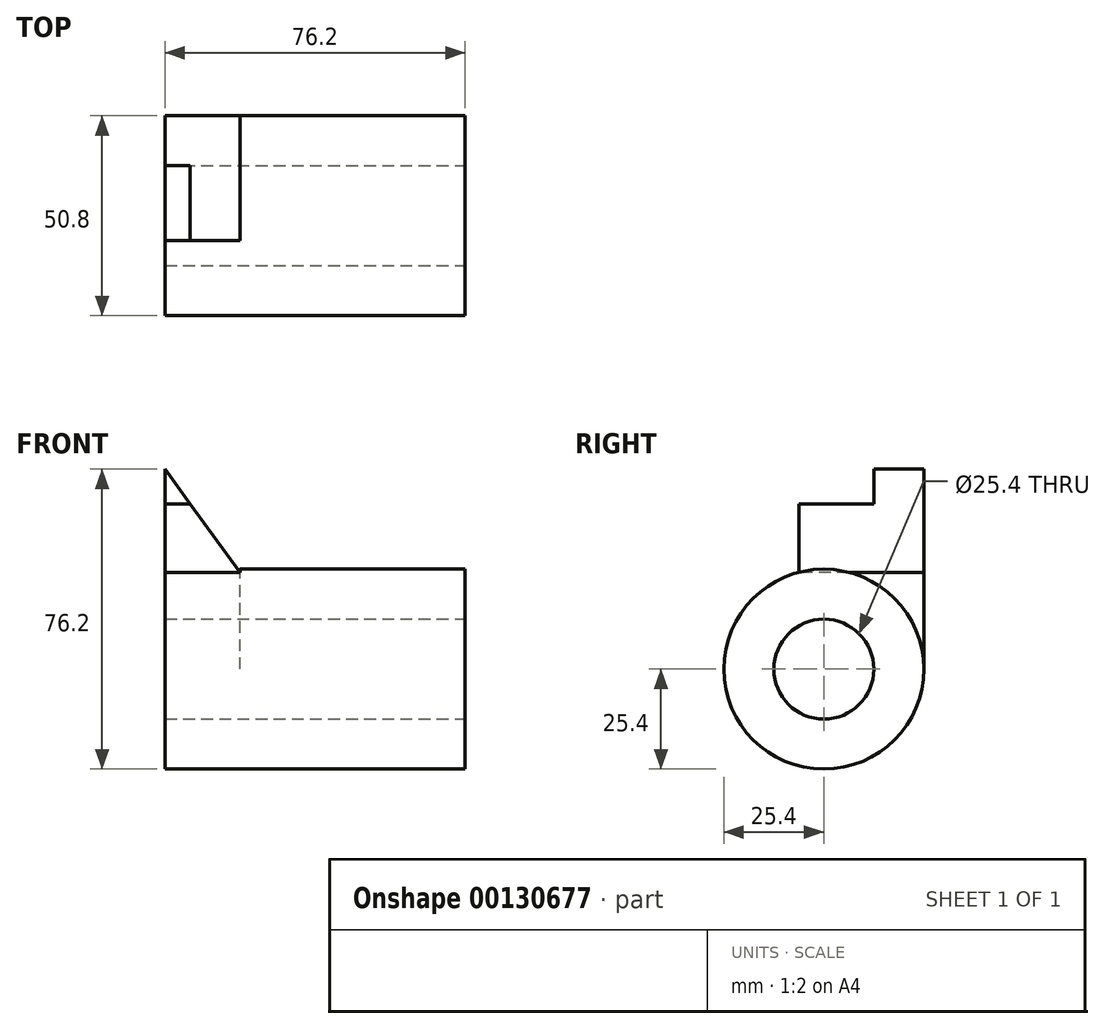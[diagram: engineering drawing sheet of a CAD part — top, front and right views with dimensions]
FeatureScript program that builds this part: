
annotation { "Feature Type Name" : "Feature", "Feature Type Description" : "" }
export const myFeature = defineFeature(function(context is Context, id is Id, definition is map)
    precondition{}
    {
        {
            var Q0;
            Q0=qCreatedBy(makeId("Front.planeOp"),FACE);
            var sketch = newSketch(context, id + "F0", { "sketchPlane" : qUnion([Q0])});
            skLineSegment(sketch, "E0.bottom", {"start": v(0, 0) * mm, "end": v(76.2, 0) * mm});
            skLineSegment(sketch, "E0.top", {"start": v(0, 76.2) * mm, "end": v(76.2, 76.2) * mm});
            skLineSegment(sketch, "E0.left", {"start": v(0, 0) * mm, "end": v(0, 76.2) * mm});
            skLineSegment(sketch, "E0.right", {"start": v(76.2, 0) * mm, "end": v(76.2, 76.2) * mm});
            skSolve(sketch);
        }
        {
            var Q0;
            Q0 = qSketchRegion(id + "F0", true);
            extrude(context, id + "F1", {"entities" : qUnion([Q0]), "depth" : 50.8 * mm});
        }
        {
            var Q0;
            Q0=makeQuery(id+"F1.opExtrude","SWEPT_FACE",FACE,{"disambiguationData":[OSD([sQuery(id+"F0.wireOp",EDGE,"E0.right")])]});
            var sketch = newSketch(context, id + "F2", { "sketchPlane" : qUnion([Q0])});
            skLineSegment(sketch, "E1", {"start": v(0, 76.2) * mm, "end": v(-12.7, 76.2) * mm});
            skLineSegment(sketch, "E2", {"start": v(-12.7, 76.2) * mm, "end": v(-12.7, 67.42) * mm});
            skLineSegment(sketch, "E3", {"start": v(-12.7, 67.42) * mm, "end": v(-31.75, 67.42) * mm});
            skCircle(sketch, "E4", {"center": v(-25.4, 25.4) * mm, "radius": 25.4 * mm});
            skPoint(sketch, "E4.centerSnap0", {"position": v(-25.4, 0) * mm});
            skLineSegment(sketch, "E5", {"start": v(-31.75, 67.42) * mm, "end": v(-31.75, 50) * mm});
            skLineSegment(sketch, "E6", {"start": v(0, 76.2) * mm, "end": v(0, 25.4) * mm});
            skLineSegment(sketch, "E7.0", {"start": v(-50.8, 0) * mm, "end": v(-50.8, 76.2) * mm});
            skLineSegment(sketch, "E8.0", {"start": v(-50.8, 0) * mm, "end": v(0, 0) * mm});
            skLineSegment(sketch, "E9", {"start": v(0, 25.4) * mm, "end": v(0, 0) * mm});
            skLineSegment(sketch, "E10", {"start": v(-50.8, 0) * mm, "end": v(-25.4, 0) * mm});
            skCircle(sketch, "E11", {"center": v(-25.4, 25.4) * mm, "radius": 12.7 * mm});
            skSolve(sketch);
        }
        {
            var Q0;
            {var subQ6=sQuery(id+"F2.wireOp",EDGE,"E2");Q0=makeQuery(id+"F2.imprint","IMPRINT",FACE,{"disambiguationData":[TD([[makeQuery(id+"F2.imprint","IMPRINT",EDGE,{"derivedFrom":subQ6}),-1.0]])]});}
            var Q1;
            {var subQ0=sQuery(id+"F2.wireOp",EDGE,"E10");Q1=makeQuery(id+"F2.imprint","IMPRINT",FACE,{"disambiguationData":[TD([[makeQuery(id+"F2.imprint","IMPRINT",EDGE,{"derivedFrom":subQ0}),1.0]])]});}
            var Q2;
            {var subQ2=sQuery(id+"F2.wireOp",EDGE,"E8.0");Q2=makeQuery(id+"F2.imprint","IMPRINT",FACE,{"disambiguationData":[TD([[makeQuery(id+"F2.imprint","IMPRINT",EDGE,{"derivedFrom":subQ2}),1.0]])]});}
            var Q3;
            Q3=makeQuery(id+"F2.imprint","IMPRINT",FACE,{"disambiguationData":[TD([[makeQuery(id+"F2.imprint","IMPRINT",EDGE,{"derivedFrom":sQuery(id+"F2.wireOp",EDGE,"E11")}),1.0]])]});
            extrude(context, id + "F3", {"entities" : qUnion([Q0, Q1, Q2, Q3]), "operationType" : NewBodyOperationType.REMOVE, "endBound" : BoundingType.THROUGH_ALL, "oppositeDirection" : true, "depth" : 25.4 * mm});
        }
        {
            var Q0;
            Q0=makeQuery(id+"F2.imprint","IMPRINT",FACE,{"disambiguationData":[TD([[makeQuery(id+"F2.imprint","IMPRINT",EDGE,{"derivedFrom":sQuery(id+"F2.wireOp",EDGE,"E1")}),-1.0]])]});
            extrude(context, id + "F4", {"entities" : qUnion([Q0]), "operationType" : NewBodyOperationType.REMOVE, "oppositeDirection" : true, "depth" : 57.15 * mm});
        }
        {
            var Q0;
            Q0=makeQuery(id+"F3.boolean.opBoolean","COPY",FACE,{"derivedFrom":makeQuery(id+"F3.opExtrude","SWEPT_FACE",FACE,{"disambiguationData":[OSD([sQuery(id+"F2.wireOp",EDGE,"E5")])]})});
            var sketch = newSketch(context, id + "F5", { "sketchPlane" : qUnion([Q0])});
            skLineSegment(sketch, "E12", {"start": v(19.05, 50) * mm, "end": v(6.35, 67.42) * mm});
            skSolve(sketch);
        }
        {
            var Q0;
            {var subQ0=sQuery(id+"F5.wireOp",EDGE,"E12");Q0=makeQuery(id+"F5.imprint","IMPRINT",FACE,{"disambiguationData":[TD([[makeQuery(id+"F5.imprint","IMPRINT",EDGE,{"derivedFrom":subQ0}),-1.0]])]});}
            extrude(context, id + "F6", {"entities" : qUnion([Q0]), "operationType" : NewBodyOperationType.REMOVE, "endBound" : BoundingType.THROUGH_ALL, "oppositeDirection" : true, "depth" : 25.4 * mm});
        }
        {
            var Q0;
            Q0=makeQuery(id+"F3.boolean.opBoolean","COPY",FACE,{"derivedFrom":makeQuery(id+"F3.opExtrude","SWEPT_FACE",FACE,{"disambiguationData":[OSD([sQuery(id+"F2.wireOp",EDGE,"E2")])]})});
            var sketch = newSketch(context, id + "F7", { "sketchPlane" : qUnion([Q0])});
            skLineSegment(sketch, "E13", {"start": v(6.35, 67.42) * mm, "end": v(0, 76.2) * mm});
            skSolve(sketch);
        }
        {
            var Q0;
            Q0=makeQuery(id+"F7.imprint","IMPRINT",FACE,{"disambiguationData":[TD([[makeQuery(id+"F7.imprint","IMPRINT",EDGE,{"derivedFrom":sQuery(id+"F7.wireOp",EDGE,"E13")}),-1.0]])]});
            extrude(context, id + "F8", {"entities" : qUnion([Q0]), "operationType" : NewBodyOperationType.REMOVE, "endBound" : BoundingType.THROUGH_ALL, "oppositeDirection" : true, "depth" : 25.4 * mm});
        }
    });
